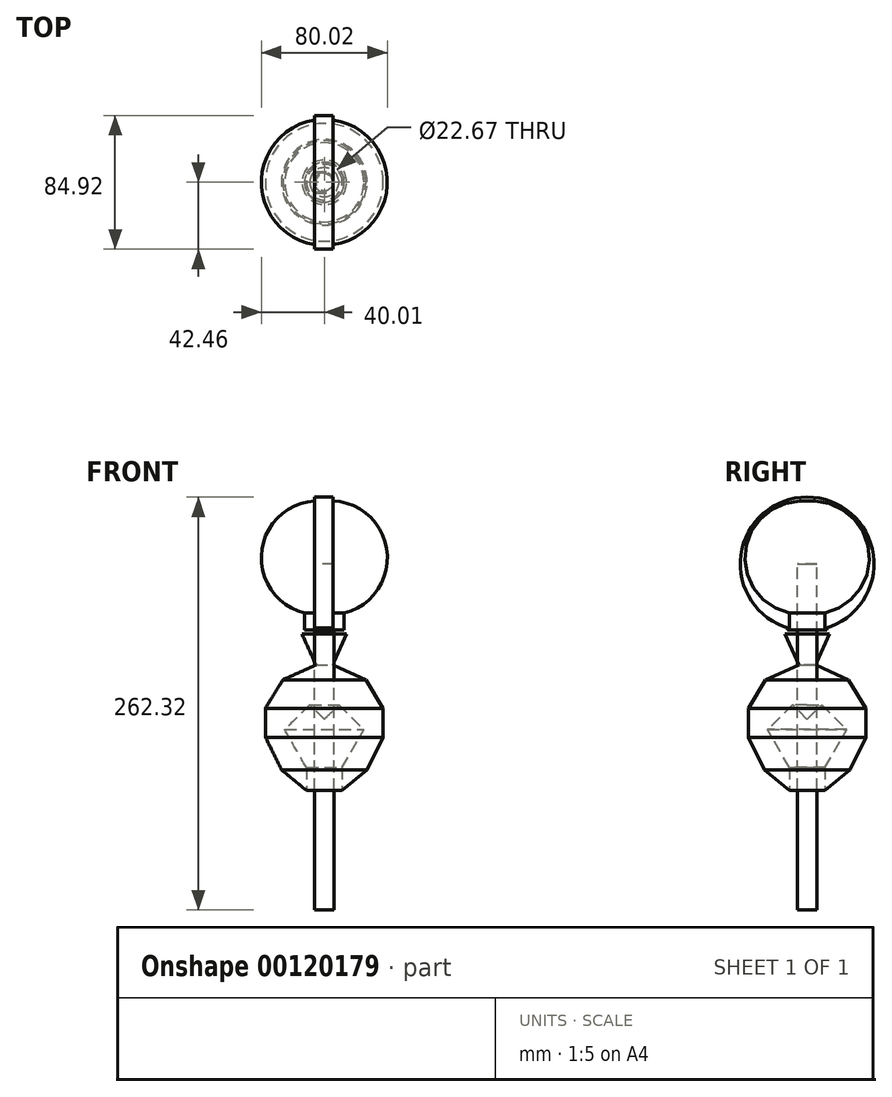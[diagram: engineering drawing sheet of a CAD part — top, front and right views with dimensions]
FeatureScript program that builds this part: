
annotation { "Feature Type Name" : "Feature", "Feature Type Description" : "" }
export const myFeature = defineFeature(function(context is Context, id is Id, definition is map)
    precondition{}
    {
        {
            var Q0;
            Q0=qCreatedBy(makeId("Front.planeOp"),FACE);
            var sketch = newSketch(context, id + "F0", { "sketchPlane" : qUnion([Q0])});
            skLineSegment(sketch, "E0", {"start": v(0, 39.93) * mm, "end": v(0, -32.09) * mm});
            skArc(sketch, "E1", {"start": v(0, 39.93) * mm, "mid": v(-40.01, 3.92) * mm, "end": v(0, -32.09) * mm});
            skSolve(sketch);
        }
        {
            var Q0;
            Q0 = qSketchRegion(id + "F0", true);
            var Q1;
            Q1=sQuery(id+"F0.wireOp",EDGE,"E0");
            revolve(context, id + "F1", {"entities" : qUnion([Q0]), "axis" : qUnion([Q1]), "revolveType" : RevolveType.FULL});
        }
        {
            var Q0;
            Q0=qCreatedBy(makeId("Front.planeOp"),FACE);
            var sketch = newSketch(context, id + "F2", { "sketchPlane" : qUnion([Q0])});
            skLineSegment(sketch, "E2", {"start": v(0, 0) * mm, "end": v(-6.17, 0) * mm});
            skLineSegment(sketch, "E3", {"start": v(-6.17, 0) * mm, "end": v(-6.17, 42.46) * mm});
            skLineSegment(sketch, "E4", {"start": v(-6.17, 42.46) * mm, "end": v(5.6, 42.46) * mm});
            skLineSegment(sketch, "E5", {"start": v(5.6, 42.46) * mm, "end": v(5.6, 0) * mm});
            skLineSegment(sketch, "E6", {"start": v(5.6, 0) * mm, "end": v(-6.17, 0) * mm});
            skSolve(sketch);
        }
        {
            var Q0;
            Q0 = qSketchRegion(id + "F2", true);
            var Q1;
            Q1=sQuery(id+"F2.wireOp",EDGE,"E6");
            revolve(context, id + "F3", {"operationType" : NewBodyOperationType.ADD, "entities" : qUnion([Q0]), "axis" : qUnion([Q1]), "revolveType" : RevolveType.FULL});
        }
        {
            var Q0;
            Q0=qCreatedBy(makeId("Top.planeOp"),FACE);
            var sketch = newSketch(context, id + "F4", { "sketchPlane" : qUnion([Q0])});
            skCircle(sketch, "E7", {"center": v(0, 0) * mm, "radius": 12.61 * mm});
            skSolve(sketch);
        }
        {
            var Q0;
            Q0 = qSketchRegion(id + "F4", true);
            extrude(context, id + "F5", {"entities" : qUnion([Q0]), "operationType" : NewBodyOperationType.ADD, "oppositeDirection" : true, "depth" : 41.9 * mm});
        }
        {
            var Q0;
            Q0=qCreatedBy(makeId("Top.planeOp"),FACE);
            var sketch = newSketch(context, id + "F6", { "sketchPlane" : qUnion([Q0])});
            skLineSegment(sketch, "E8.bottom", {"start": v(-6.17, 6.3) * mm, "end": v(5.6, 6.3) * mm});
            skLineSegment(sketch, "E8.top", {"start": v(-6.17, -6.3) * mm, "end": v(5.6, -6.3) * mm});
            skLineSegment(sketch, "E8.left", {"start": v(-6.17, 6.3) * mm, "end": v(-6.17, -6.3) * mm});
            skLineSegment(sketch, "E8.right", {"start": v(5.6, 6.3) * mm, "end": v(5.6, -6.3) * mm});
            skSolve(sketch);
        }
        {
            var Q0;
            Q0 = qSketchRegion(id + "F6", true);
            extrude(context, id + "F7", {"entities" : qUnion([Q0]), "operationType" : NewBodyOperationType.ADD, "oppositeDirection" : true, "depth" : 44.1 * mm});
        }
        {
            var Q0;
            Q0=qCreatedBy(makeId("Right.planeOp"),FACE);
            var sketch = newSketch(context, id + "F8", { "sketchPlane" : qUnion([Q0])});
            skLineSegment(sketch, "E9", {"start": v(0, -44.52) * mm, "end": v(-14.15, -44.52) * mm});
            skLineSegment(sketch, "E10", {"start": v(-14.15, -44.52) * mm, "end": v(-5.36, -64.22) * mm});
            skLineSegment(sketch, "E11", {"start": v(-5.36, -64.22) * mm, "end": v(-26.36, -73.6) * mm});
            skLineSegment(sketch, "E12", {"start": v(-26.36, -73.6) * mm, "end": v(-37.4, -91.74) * mm});
            skLineSegment(sketch, "E13", {"start": v(-37.4, -91.74) * mm, "end": v(-37.4, -110.06) * mm});
            skLineSegment(sketch, "E14", {"start": v(-37.4, -110.06) * mm, "end": v(-27.19, -130.78) * mm});
            skLineSegment(sketch, "E15", {"start": v(-27.19, -130.78) * mm, "end": v(-11.33, -143.88) * mm});
            skLineSegment(sketch, "E16", {"start": v(-11.33, -143.88) * mm, "end": v(-11.33, -129.4) * mm});
            skLineSegment(sketch, "E17", {"start": v(-11.33, -129.4) * mm, "end": v(-25.12, -105.27) * mm});
            skLineSegment(sketch, "E18", {"start": v(-25.12, -105.27) * mm, "end": v(-9.27, -89.42) * mm});
            skLineSegment(sketch, "E19", {"start": v(-9.27, -89.42) * mm, "end": v(0, -98.68) * mm});
            skLineSegment(sketch, "E20", {"start": v(0, -98.68) * mm, "end": v(0, -44.52) * mm});
            skPoint(sketch, "E21.orphan", {"position": v(0, -76.23) * mm});
            skSolve(sketch);
        }
        {
            var Q0;
            Q0 = qSketchRegion(id + "F8", true);
            var Q1;
            Q1=makeQuery(id+"F5.opExtrude","CAP_EDGE",EDGE,{"disambiguationData":[OSD([sQuery(id+"F4.wireOp",EDGE,"E7")])],"isStart":false});
            revolve(context, id + "F9", {"entities" : qUnion([Q0]), "axis" : qUnion([Q1]), "revolveType" : RevolveType.FULL});
        }
        {
            var Q0;
            Q0=qCreatedBy(makeId("Top.planeOp"),FACE);
            var sketch = newSketch(context, id + "F10", { "sketchPlane" : qUnion([Q0])});
            skCircle(sketch, "E22", {"center": v(0, 0) * mm, "radius": 6.26 * mm});
            skSolve(sketch);
        }
        {
            var Q0;
            Q0 = qSketchRegion(id + "F10", true);
            extrude(context, id + "F11", {"entities" : qUnion([Q0]), "endBound" : BoundingType.THROUGH_ALL, "oppositeDirection" : true, "depth" : 58.6 * mm});
        }
    });
